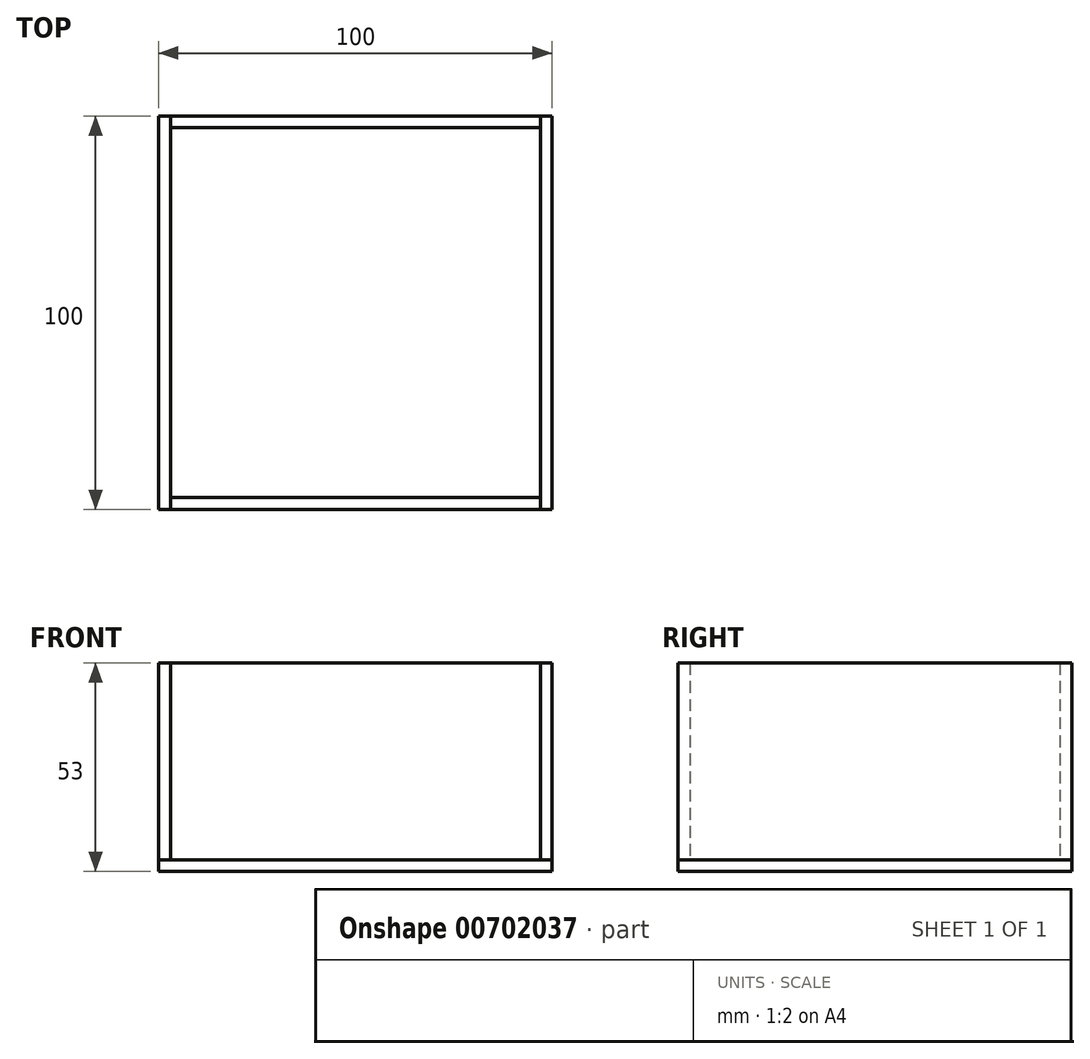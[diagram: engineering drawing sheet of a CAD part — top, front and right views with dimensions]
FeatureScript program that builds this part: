
annotation { "Feature Type Name" : "Feature", "Feature Type Description" : "" }
export const myFeature = defineFeature(function(context is Context, id is Id, definition is map)
    precondition{}
    {
        {
            var Q0;
            Q0=qCreatedBy(makeId("Top.planeOp"),FACE);
            var sketch = newSketch(context, id + "F0", { "sketchPlane" : qUnion([Q0])});
            skLineSegment(sketch, "E0.bottom", {"start": v(50, -50) * mm, "end": v(-50, -50) * mm});
            skLineSegment(sketch, "E0.top", {"start": v(50, 50) * mm, "end": v(-50, 50) * mm});
            skLineSegment(sketch, "E0.left", {"start": v(50, -50) * mm, "end": v(50, 50) * mm});
            skLineSegment(sketch, "E0.right", {"start": v(-50, -50) * mm, "end": v(-50, 50) * mm});
            skPoint(sketch, "E0.middle", {"position": v(0, 0) * mm});
            skSolve(sketch);
        }
        {
            var Q0;
            Q0 = qSketchRegion(id + "F0", true);
            extrude(context, id + "F1", {"entities" : qUnion([Q0]), "depth" : 3 * mm, "offsetDistance" : 25 * mm});
        }
        {
            var Q0;
            Q0=makeQuery(id+"F1.opExtrude","CAP_FACE",FACE,{"disambiguationData":[OSD([sQuery(id+"F0.wireOp",EDGE,"E0.bottom"),sQuery(id+"F0.wireOp",EDGE,"E0.top"),sQuery(id+"F0.wireOp",EDGE,"E0.left"),sQuery(id+"F0.wireOp",EDGE,"E0.right")])],"isStart":false});
            var sketch = newSketch(context, id + "F2", { "sketchPlane" : qUnion([Q0])});
            skLineSegment(sketch, "E1.bottom", {"start": v(47, -47) * mm, "end": v(-47, -47) * mm});
            skLineSegment(sketch, "E1.top", {"start": v(47, 47) * mm, "end": v(-47, 47) * mm});
            skLineSegment(sketch, "E1.left", {"start": v(47, -47) * mm, "end": v(47, 47) * mm});
            skLineSegment(sketch, "E1.right", {"start": v(-47, -47) * mm, "end": v(-47, 47) * mm});
            skPoint(sketch, "E1.middle", {"position": v(0, 0) * mm});
            skLineSegment(sketch, "E2.bottom", {"start": v(50, -50) * mm, "end": v(-50, -50) * mm});
            skLineSegment(sketch, "E2.top", {"start": v(50, 50) * mm, "end": v(-50, 50) * mm});
            skLineSegment(sketch, "E2.left", {"start": v(50, -50) * mm, "end": v(50, 50) * mm});
            skLineSegment(sketch, "E2.right", {"start": v(-50, -50) * mm, "end": v(-50, 50) * mm});
            skLineSegment(sketch, "E3", {"start": v(-47, 47) * mm, "end": v(-47, 50) * mm});
            skLineSegment(sketch, "E4", {"start": v(47, 47) * mm, "end": v(47, 50) * mm});
            skLineSegment(sketch, "E5", {"start": v(47, -47) * mm, "end": v(47, -50) * mm});
            skLineSegment(sketch, "E6", {"start": v(-47, -47) * mm, "end": v(-47, -50) * mm});
            skSolve(sketch);
        }
        {
            var Q0;
            Q0=makeQuery(id+"F2.imprint","IMPRINT",FACE,{"disambiguationData":[TD([[makeQuery(id+"F2.imprint","IMPRINT",EDGE,{"derivedFrom":sQuery(id+"F2.wireOp",EDGE,"E1.top")}),-1.0]])]});
            var Q1;
            Q1=makeQuery(id+"F2.imprint","IMPRINT",FACE,{"disambiguationData":[TD([[makeQuery(id+"F2.imprint","IMPRINT",EDGE,{"derivedFrom":sQuery(id+"F2.wireOp",EDGE,"E1.bottom")}),1.0]])]});
            extrude(context, id + "F3", {"entities" : qUnion([Q0, Q1]), "depth" : 50 * mm, "offsetDistance" : 25 * mm});
        }
        {
            var Q0;
            Q0=makeQuery(id+"F2.imprint","IMPRINT",FACE,{"disambiguationData":[TD([[makeQuery(id+"F2.imprint","IMPRINT",EDGE,{"derivedFrom":sQuery(id+"F2.wireOp",EDGE,"E1.right")}),1.0]])]});
            var Q1;
            Q1=makeQuery(id+"F2.imprint","IMPRINT",FACE,{"disambiguationData":[TD([[makeQuery(id+"F2.imprint","IMPRINT",EDGE,{"derivedFrom":sQuery(id+"F2.wireOp",EDGE,"E1.left")}),-1.0]])]});
            extrude(context, id + "F4", {"entities" : qUnion([Q0, Q1]), "depth" : 50 * mm, "offsetDistance" : 25 * mm});
        }
    });
